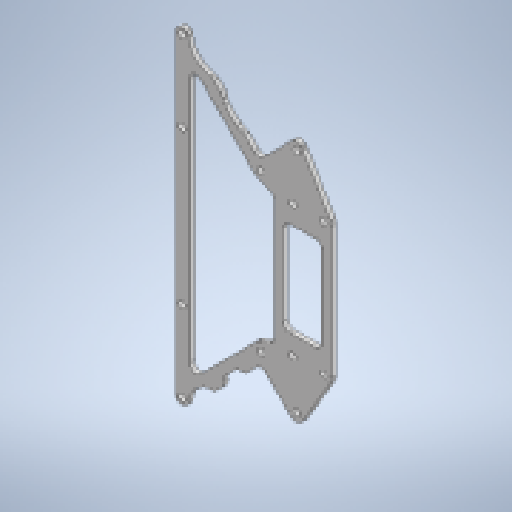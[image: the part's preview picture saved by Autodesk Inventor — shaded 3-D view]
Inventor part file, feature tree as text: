
AUTODESK INVENTOR PART (.ipt)
format: ipt  version: 2025.1 (Build 291241000, 241)  size: 301,568 bytes
history: native  units: mm
features: reference x15, other x8, extrude x5, sketch x5, fillet x4
ambient origin geometry x8: Origin, YZ Plane, XZ Plane, XY Plane, X Axis, Y Axis, Z Axis, Center Point
bodies: Body1 (feature_tree)
feature tree (37):
  other  "ソリッド1"
  extrude  "押し出し1"  Depth=2.2mm
  fillet  "フィレット1"  Radius=4.0mm
  extrude  "押し出し2"  Depth=1.5mm TaperAngle=0.0deg
  fillet  "フィレット2"  Radius=2.0mm
  extrude  "押し出し3"  Depth=1.0mm
  fillet  "フィレット3"  Radius=2.0mm
  extrude  "押し出し4"  Depth=2.0mm
  fillet  "フィレット4"  Radius=1.0mm
  extrude  "押し出し5"  TaperAngle=0.0deg  [1 undecoded]
  sketch  "スケッチ1"
  reference  "参照1"
  reference  "参照2"
  reference  "参照3"
  sketch  "スケッチ2"
  reference  "参照4"
  reference  "参照5"
  reference  "参照6"
  reference  "参照7"
  reference  "参照8"
  reference  "参照9"
  reference  "参照10"
  reference  "参照11"
  reference  "参照12"
  sketch  "スケッチ3"
  reference  "参照13"
  sketch  "スケッチ4"
  sketch  "スケッチ5"
  reference  "参照14"
  reference  "参照15"
  other  "Assembly1"
  other  "piti_mata:3"
  other  "<userpath>\Documents\Inventor\Vixen\kosi_v2.iam"
  other  "kosi_v2.iam"
  other  "piti_mata:1"
  other  "KRS2500_scale:1"
  other  "KRS2500_scale:2"
note: 1 required parameter value undecoded (feature->parameter linkage not recoverable at this tier; creation-order binding heuristic only, values carry confidence <= 0.55)
